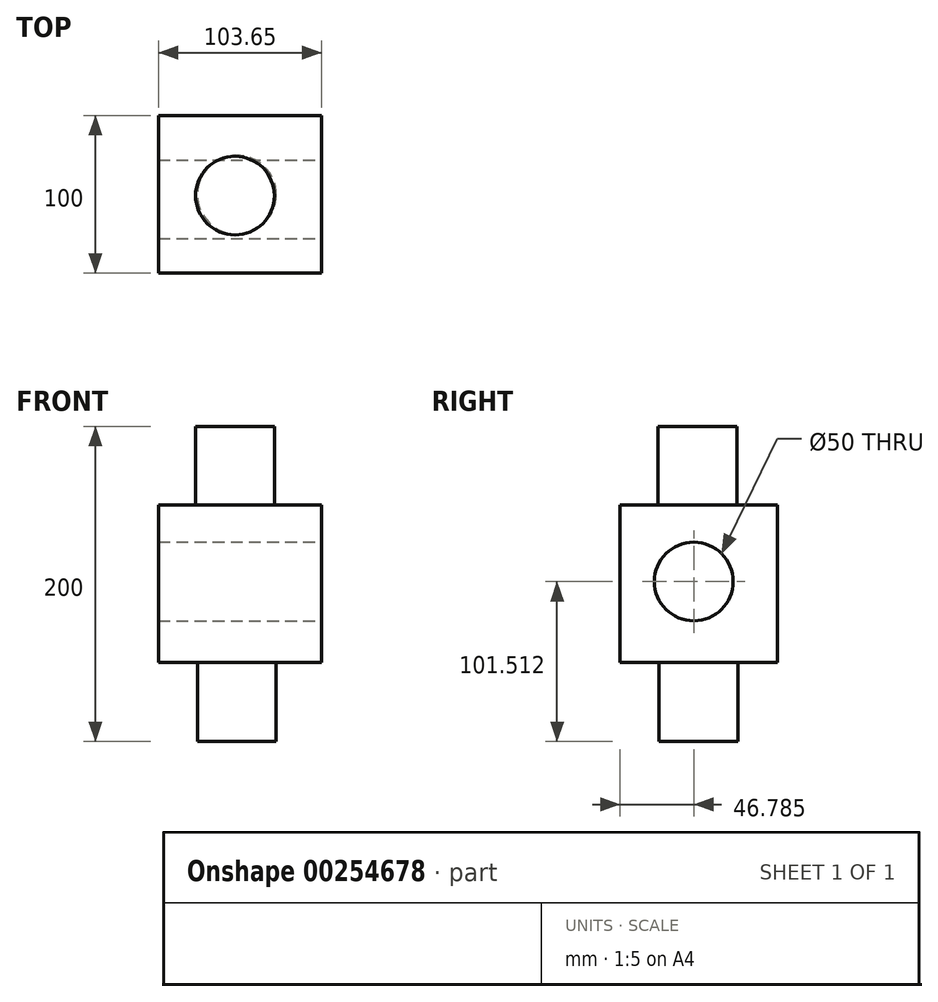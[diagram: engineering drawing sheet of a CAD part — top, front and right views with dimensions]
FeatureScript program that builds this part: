
annotation { "Feature Type Name" : "Feature", "Feature Type Description" : "" }
export const myFeature = defineFeature(function(context is Context, id is Id, definition is map)
    precondition{}
    {
        {
            var Q0;
            Q0=qCreatedBy(makeId("Front.planeOp"),FACE);
            var sketch = newSketch(context, id + "F0", { "sketchPlane" : qUnion([Q0])});
            skLineSegment(sketch, "E0.bottom", {"start": v(0, 0) * mm, "end": v(103.65, 0) * mm});
            skLineSegment(sketch, "E0.top", {"start": v(0, 100) * mm, "end": v(103.65, 100) * mm});
            skLineSegment(sketch, "E0.left", {"start": v(0, 0) * mm, "end": v(0, 100) * mm});
            skLineSegment(sketch, "E0.right", {"start": v(103.65, 0) * mm, "end": v(103.65, 100) * mm});
            skSolve(sketch);
        }
        {
            var Q0;
            Q0=makeQuery(id+"F0.imprint","IMPRINT",FACE,{"disambiguationData":[TD([[makeQuery(id+"F0.imprint","IMPRINT",EDGE,{"derivedFrom":sQuery(id+"F0.wireOp",EDGE,"E0.bottom")}),1.0]])]});
            var sketch = newSketch(context, id + "F1", { "sketchPlane" : qUnion([Q0])});
            skSolve(sketch);
        }
        {
            var Q0;
            Q0=makeQuery(id+"F1.imprint","IMPRINT",FACE,{"disambiguationData":[TD([[makeQuery(id+"F1.imprint","IMPRINT",EDGE,{"derivedFrom":makeQuery(id+"F0.imprint","IMPRINT",EDGE,{"derivedFrom":sQuery(id+"F0.wireOp",EDGE,"E0.bottom")})}),1.0]])]});
            extrude(context, id + "F2", {"entities" : qUnion([Q0]), "depth" : 100 * mm});
        }
        {
            var Q0;
            Q0=makeQuery(id+"F2.opExtrude","SWEPT_FACE",FACE,{"disambiguationData":[OSD([sQuery(id+"F0.wireOp",EDGE,"E0.top")])]});
            var sketch = newSketch(context, id + "F3", { "sketchPlane" : qUnion([Q0])});
            skCircle(sketch, "E1", {"center": v(48.63, -50.88) * mm, "radius": 25 * mm});
            skSolve(sketch);
        }
        {
            var Q0;
            Q0=makeQuery(id+"F2.opExtrude","SWEPT_FACE",FACE,{"disambiguationData":[OSD([sQuery(id+"F0.wireOp",EDGE,"E0.bottom")])]});
            var sketch = newSketch(context, id + "F4", { "sketchPlane" : qUnion([Q0])});
            skCircle(sketch, "E2", {"center": v(49.75, 50.3) * mm, "radius": 25 * mm});
            skSolve(sketch);
        }
        {
            var Q0;
            Q0=makeQuery(id+"F2.opExtrude","SWEPT_FACE",FACE,{"disambiguationData":[OSD([sQuery(id+"F0.wireOp",EDGE,"E0.right")])]});
            var sketch = newSketch(context, id + "F5", { "sketchPlane" : qUnion([Q0])});
            skPoint(sketch, "E3", {"position": v(-53.22, 51.51) * mm});
            skSolve(sketch);
        }
        {
            var Q0;
            Q0=sQuery(id+"F5.wireOp",VERTEX,"E3");
            var Q1;
            Q1=makeQuery(id+"F2.opExtrude","SWEPT_BODY",BODY,{"disambiguationData":[OSD([sQuery(id+"F0.wireOp",EDGE,"E0.bottom"),sQuery(id+"F0.wireOp",EDGE,"E0.top"),sQuery(id+"F0.wireOp",EDGE,"E0.left"),sQuery(id+"F0.wireOp",EDGE,"E0.right")])]});
            hole(context, id + "F6", {"style" : HoleStyle.SIMPLE, "endStyle" : HoleEndStyle.THROUGH, "holeDiameter" : 50 * mm, "tappedDepth" : 12 * mm, "tapClearance" : 3, "locations" : qUnion([Q0]), "scope" : qUnion([Q1])});
        }
        {
            var Q0;
            Q0=makeQuery(id+"F3.imprint","IMPRINT",FACE,{"disambiguationData":[TD([[makeQuery(id+"F3.imprint","IMPRINT",EDGE,{"derivedFrom":sQuery(id+"F3.wireOp",EDGE,"E1")}),1.0]])]});
            extrude(context, id + "F7", {"entities" : qUnion([Q0]), "operationType" : NewBodyOperationType.ADD, "depth" : 50 * mm});
        }
        {
            var Q0;
            Q0=makeQuery(id+"F4.imprint","IMPRINT",FACE,{"disambiguationData":[TD([[makeQuery(id+"F4.imprint","IMPRINT",EDGE,{"derivedFrom":sQuery(id+"F4.wireOp",EDGE,"E2")}),1.0]])]});
            extrude(context, id + "F8", {"entities" : qUnion([Q0]), "operationType" : NewBodyOperationType.ADD, "depth" : 50 * mm});
        }
    });
